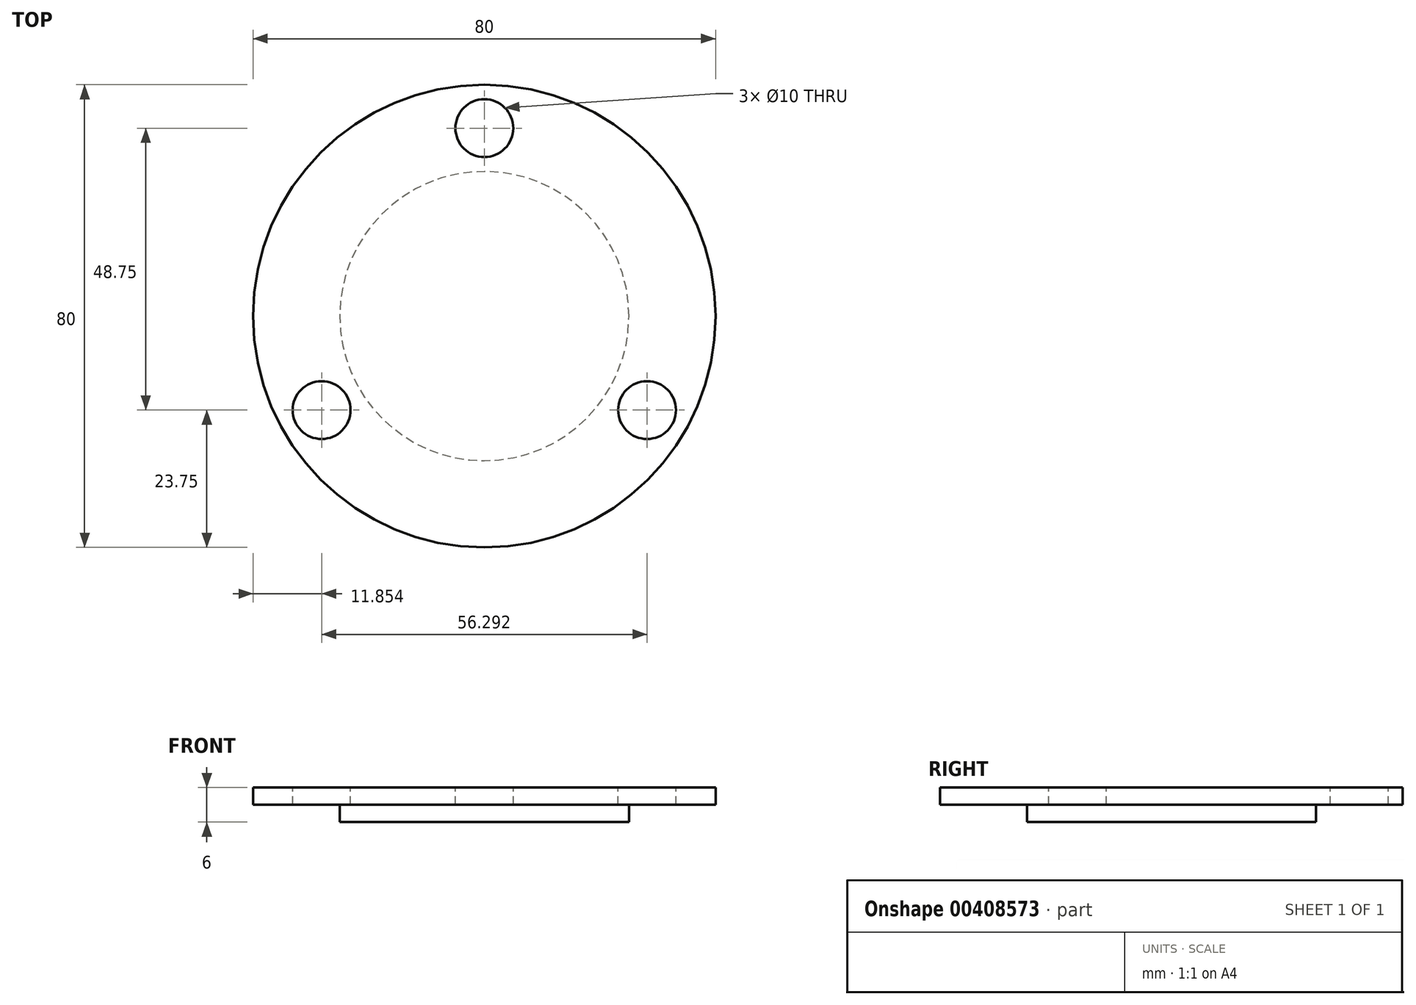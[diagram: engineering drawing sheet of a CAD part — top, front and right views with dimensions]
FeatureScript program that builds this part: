
annotation { "Feature Type Name" : "Feature", "Feature Type Description" : "" }
export const myFeature = defineFeature(function(context is Context, id is Id, definition is map)
    precondition{}
    {
        {
            var Q0;
            Q0=qCreatedBy(makeId("Top.planeOp"),FACE);
            var sketch = newSketch(context, id + "F0", { "sketchPlane" : qUnion([Q0])});
            skCircle(sketch, "E0", {"center": v(0, 0) * mm, "radius": 40 * mm});
            skSolve(sketch);
        }
        {
            var Q0;
            Q0=makeQuery(id+"F0.imprint","IMPRINT",FACE,{"disambiguationData":[TD([[makeQuery(id+"F0.imprint","IMPRINT",EDGE,{"derivedFrom":sQuery(id+"F0.wireOp",EDGE,"E0")}),1.0]])]});
            extrude(context, id + "F1", {"entities" : qUnion([Q0]), "oppositeDirection" : true, "depth" : 3 * mm, "offsetDistance" : 25 * mm});
        }
        {
            var Q0;
            Q0=qCreatedBy(makeId("Top.planeOp"),FACE);
            var sketch = newSketch(context, id + "F2", { "sketchPlane" : qUnion([Q0])});
            skCircle(sketch, "E1", {"center": v(0, 32.5) * mm, "radius": 5 * mm});
            skLineSegment(sketch, "E2", {"start": v(0, 0) * mm, "end": v(-5.27, -3.04) * mm, "construction": true});
            skLineSegment(sketch, "E3", {"start": v(0, 0) * mm, "end": v(6.22, -3.6) * mm, "construction": true});
            skCircle(sketch, "E4", {"center": v(-28.15, -16.25) * mm, "radius": 5 * mm});
            skCircle(sketch, "E5", {"center": v(28.15, -16.25) * mm, "radius": 5 * mm});
            skSolve(sketch);
        }
        {
            var Q0;
            Q0=makeQuery(id+"F2.imprint","IMPRINT",FACE,{"disambiguationData":[TD([[makeQuery(id+"F2.imprint","IMPRINT",EDGE,{"derivedFrom":sQuery(id+"F2.wireOp",EDGE,"E1")}),1.0]])]});
            var Q1;
            Q1=makeQuery(id+"F2.imprint","IMPRINT",FACE,{"disambiguationData":[TD([[makeQuery(id+"F2.imprint","IMPRINT",EDGE,{"derivedFrom":sQuery(id+"F2.wireOp",EDGE,"E4")}),1.0]])]});
            var Q2;
            Q2=makeQuery(id+"F2.imprint","IMPRINT",FACE,{"disambiguationData":[TD([[makeQuery(id+"F2.imprint","IMPRINT",EDGE,{"derivedFrom":sQuery(id+"F2.wireOp",EDGE,"E5")}),1.0]])]});
            extrude(context, id + "F3", {"entities" : qUnion([Q0, Q1, Q2]), "operationType" : NewBodyOperationType.REMOVE, "oppositeDirection" : true, "depth" : 25 * mm, "offsetDistance" : 25 * mm});
        }
        {
            var Q0;
            Q0=makeQuery(id+"F1.opExtrude","CAP_FACE",FACE,{"disambiguationData":[OSD([sQuery(id+"F0.wireOp",EDGE,"E0")])],"isStart":false});
            var sketch = newSketch(context, id + "F4", { "sketchPlane" : qUnion([Q0])});
            skCircle(sketch, "E6", {"center": v(0, 0) * mm, "radius": 25 * mm});
            skSolve(sketch);
        }
        {
            var Q0;
            Q0 = qSketchRegion(id + "F4", true);
            extrude(context, id + "F5", {"entities" : qUnion([Q0]), "operationType" : NewBodyOperationType.ADD, "depth" : 3 * mm, "offsetDistance" : 25 * mm});
        }
    });
